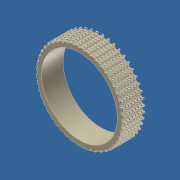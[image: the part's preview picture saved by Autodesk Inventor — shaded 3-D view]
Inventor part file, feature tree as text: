
AUTODESK INVENTOR PART (.ipt)
format: ipt  version: 2011 (Build 150239000, 239)  size: 3,572,224 bytes
history: native  units: in
note: dims shown in document units (in); Inventor stores cm internally (conversion verified against a paired STEP export)
features: extrude x2, sketch x2, pattern_circular x1, pattern_linear x1
ambient origin geometry x8: Origin, YZ Plane, XZ Plane, XY Plane, X Axis, Y Axis, Z Axis, Center Point
bodies: Solid1 (feature_tree)
feature tree (6):
  extrude  "Extrusion1"  Depth=0.05in
  extrude  "Extrusion2"  Depth=2.0in
  pattern_circular  "Circular Pattern2"  [2 undecoded]
  pattern_linear  "Rectangular Pattern1"  Spacing1=0.292in  [1 undecoded]
  sketch  "Sketch1"  dims[d0=0.0515in d1=0.05in]
  sketch  "Sketch2"  dims[d2=0.05in d3=2.0in d4=0.0714in d5=0.0in d6=0.292in d7=0.106in d9=0.106in d10=0.0714in d11=0.0in d15=18.8976in d16=360.0deg d18=2.7559in d20=0.1429in]
note: 3 required parameter values undecoded (feature->parameter linkage not recoverable at this tier; creation-order binding heuristic only, values carry confidence <= 0.55)
